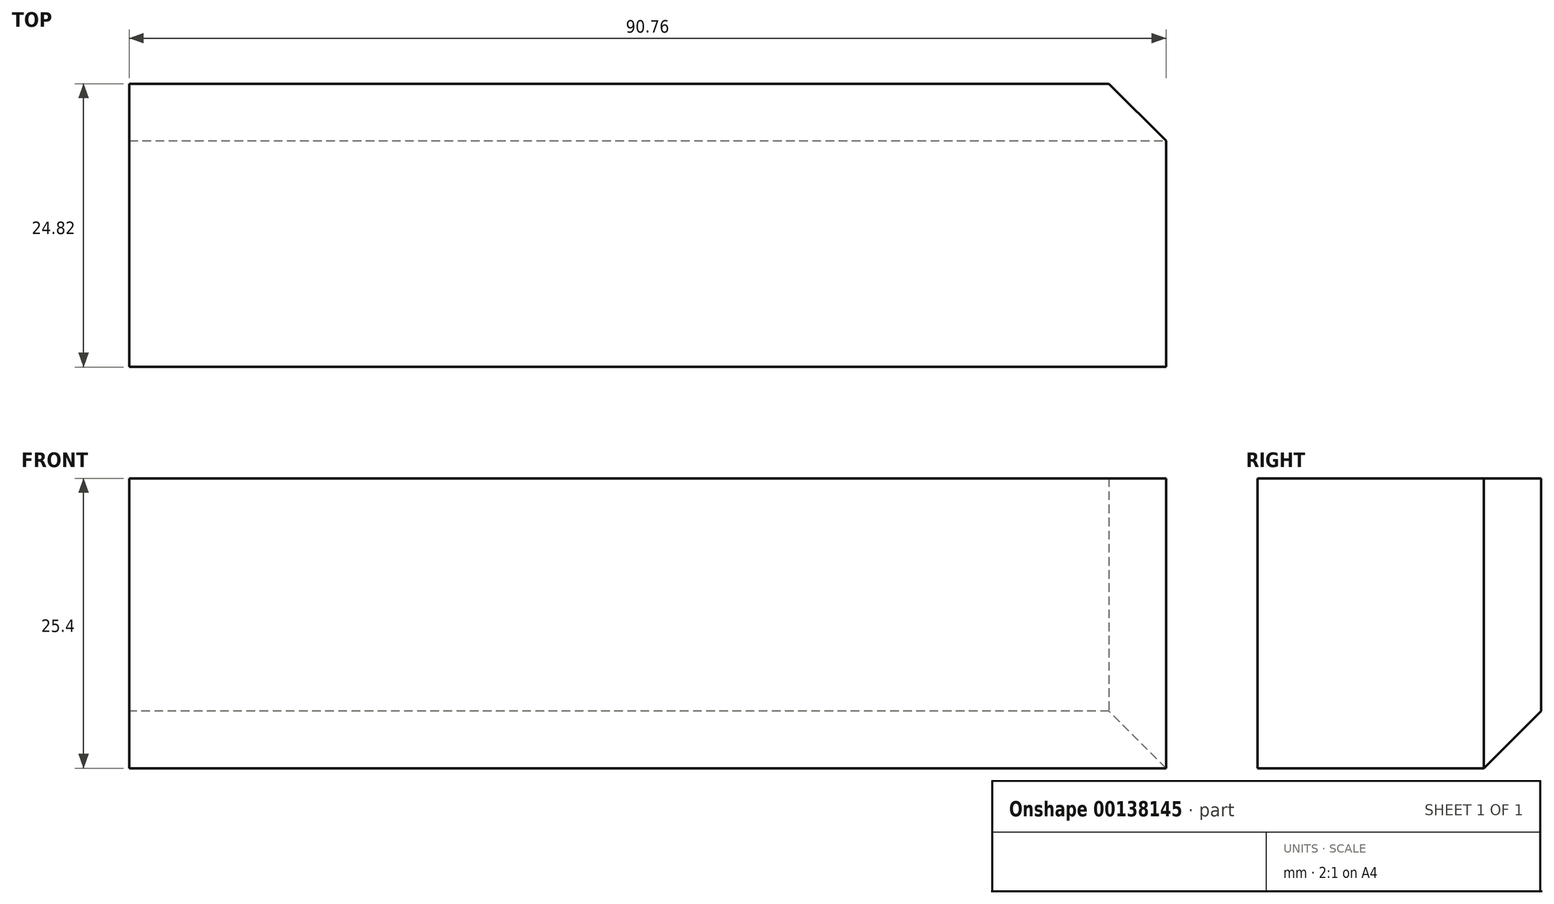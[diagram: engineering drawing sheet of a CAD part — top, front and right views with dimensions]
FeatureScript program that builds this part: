
annotation { "Feature Type Name" : "Feature", "Feature Type Description" : "" }
export const myFeature = defineFeature(function(context is Context, id is Id, definition is map)
    precondition{}
    {
        {
            var Q0;
            Q0=qCreatedBy(makeId("Top.planeOp"),FACE);
            var sketch = newSketch(context, id + "F1", { "sketchPlane" : qUnion([Q0])});
            skLineSegment(sketch, "E0.bottom", {"start": v(-40.15, 39.08) * mm, "end": v(50.6, 39.08) * mm});
            skLineSegment(sketch, "E0.top", {"start": v(-40.15, 14.26) * mm, "end": v(50.6, 14.26) * mm});
            skLineSegment(sketch, "E0.left", {"start": v(-40.15, 39.08) * mm, "end": v(-40.15, 14.26) * mm});
            skLineSegment(sketch, "E0.right", {"start": v(50.6, 39.08) * mm, "end": v(50.6, 14.26) * mm});
            skSolve(sketch);
        }
        {
            var Q0;
            Q0=makeQuery(id+"F1.imprint","IMPRINT",FACE,{"disambiguationData":[TD([[makeQuery(id+"F1.imprint","IMPRINT",EDGE,{"derivedFrom":sQuery(id+"F1.wireOp",EDGE,"E0.bottom")}),-1.0]])]});
            var Q1;
            Q1=sQuery(id+"F1.wireOp",EDGE,"E0.top");
            extrude(context, id + "F2", {"entities" : qUnion([Q0]), "surfaceEntities" : qUnion([Q1]), "depth" : 25.4 * mm});
        }
        {
            var Q0;
            Q0=makeQuery(id+"F2.opExtrude","CAP_EDGE",EDGE,{"disambiguationData":[OSD([sQuery(id+"F1.wireOp",EDGE,"E0.bottom")])],"isStart":true});
            var Q1;
            Q1=makeQuery(id+"F2.opExtrude","SWEPT_EDGE",EDGE,{"disambiguationData":[OSD([sQuery(id+"F1.wireOp",EDGE,"E0.bottom"),sQuery(id+"F1.wireOp",EDGE,"E0.right")])]});
            chamfer(context, id + "F3", {"entities" : qUnion([Q0, Q1]), "width" : 5 * mm, "tangentPropagation" : true});
        }
    });
